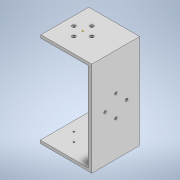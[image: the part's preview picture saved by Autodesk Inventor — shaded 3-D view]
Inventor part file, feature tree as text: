
AUTODESK INVENTOR PART (.ipt)
format: ipt  version: 2022.2 (Build 262287030, 287C)  size: 176,128 bytes
history: native  units: in
note: dims shown in document units (in); Inventor stores cm internally (conversion verified against a paired STEP export)
features: sketch x4, hole x3, extrude x1
ambient origin geometry x8: Origin, YZ Plane, XZ Plane, XY Plane, X Axis, Y Axis, Z Axis, Center Point
bodies: Solid1 (feature_tree)
feature tree (8):
  extrude  "Extrusion1"  TaperAngle=90.0deg  [1 undecoded]
  sketch  "Sketch3"  dims[d2=3.1496in d3=90.0deg]
  hole  "Hole2"  [1 undecoded]
  hole  "Hole3"  [1 undecoded]
  hole  "Hole4"  [1 undecoded]
  sketch  "Sketch1"  dims[d0=5.8268in d1=90.0deg]
  sketch  "Sketch5"  dims[d4=0.1969in d5=90.0deg]
  sketch  "Sketch6"  dims[d6=3.3858in d7=90.0deg d8=6.2205in d9=90.0deg d10=3.3465in d11=90.0deg d12=0.1969in d13=90.0deg d14=3.1496in d15=0.0in d30=90.0deg d31=2.1654in d32=1.5748in d33=0.5906in d34=1.5748in d36=360.0deg d38=0.0968in d39=0.2362in d40=0.2362in d41=0.0394in d42=90.0deg d43=0.3937in d44=0.8108in d45=2.8543in d48=90.0deg d49=2.1654in d50=0.5906in d51=1.5748in d53=360.0deg d55=0.0968in d56=0.2362in d57=0.2362in d58=0.0394in d59=90.0deg d60=0.3937in d61=0.0in d62=0.7098in d63=1.5748in d65=360.0deg d67=0.1628in d68=0.0004in d69=0.3909in d70=0.1181in d71=90.0deg d72=0.3937in d73=0.0in d46=0.8108in d47=0.0246in d64=0.3937in d66=0.0984in]
note: 4 required parameter values undecoded (feature->parameter linkage not recoverable at this tier; creation-order binding heuristic only, values carry confidence <= 0.55)
